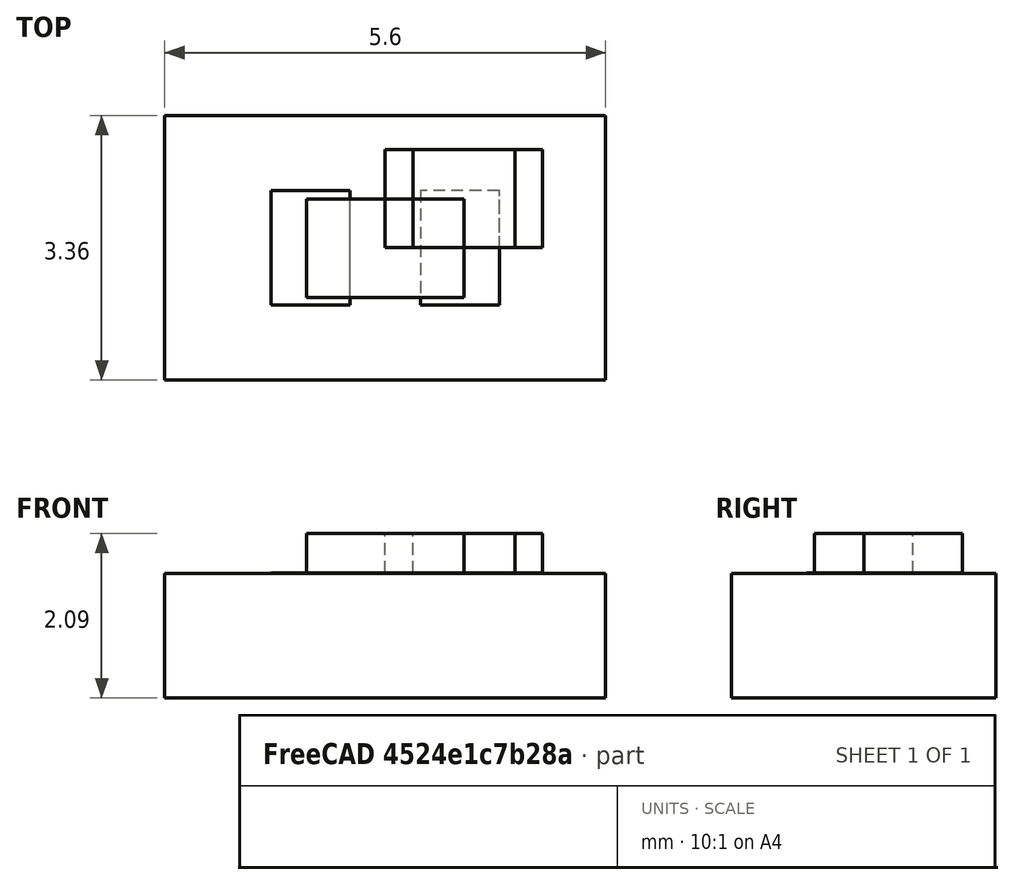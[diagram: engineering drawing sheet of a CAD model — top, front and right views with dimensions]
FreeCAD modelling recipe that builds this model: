
FCSTD DOCUMENT  (FreeCAD 0.17R13541 (Git))
Label: RESC2012X100N
License: All rights reserved
LicenseURL: http://en.wikipedia.org/wiki/All_rights_reserved
objects: Part::FeaturePython×4, Part::Box×3, App::DocumentObjectGroup×1, Part::Feature×1
note: 8 computed .brp shape members not serialized (recipe doc carries the construction recipe); baked Part::Feature solids carry a one-line shape summary decoded from their .brp

FEATURE [Part::Box] Box  label="pad1"
  AttacherType = Attacher::AttachEngine3D
  Height = 0.5
  Length = 0.35
  Width = 1.25
FEATURE [Part::Box] Box001  label="body"
  AttacherType = Attacher::AttachEngine3D
  Height = 0.5
  Length = 1.3
  Placement = pos=(0.35,0,0) rot=(0,0,1;0rad)
  Width = 1.25
  expr: Length = 2 - 0.34999999999999998 - 0.34999999999999998
FEATURE [Part::Box] Box002  label="pad2"
  AttacherType = Attacher::AttachEngine3D
  Height = 0.5
  Length = 0.35
  Placement = pos=(1.65,0,0) rot=(0,0,1;0rad)
  Width = 1.25
  expr: Placement.Base.x = 2 - 0.34999999999999998
FEATURE [Part::FeaturePython] FCrtYd_lines  label="FCrtYd"  # a2plus imported part (geometry in sourceFile) (typed FeaturePython)
  fixedPosition = true
FEATURE [Part::FeaturePython] Filk_lines  label="FrontSilk"  # a2plus imported part (geometry in sourceFile) (typed FeaturePython)
  fixedPosition = true
FEATURE [Part::FeaturePython] TopPads  # a2plus imported part (geometry in sourceFile) (typed FeaturePython)
  fixedPosition = true
FEATURE [Part::FeaturePython] newPCB  label="Pcb"  # a2plus imported part (geometry in sourceFile) (typed FeaturePython)
  fixedPosition = true
FEATURE [App::DocumentObjectGroup] RESC2012X100N_fp
  Group = -> [FCrtYd_lines,Filk_lines,TopPads,newPCB]
FEATURE [Part::Feature] Shape001  label="RESC2012X100N"
  shape: bbox 2 x 1.25 x 0.5 mm, 14 faces (baked)
